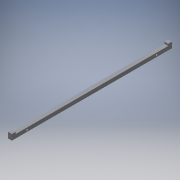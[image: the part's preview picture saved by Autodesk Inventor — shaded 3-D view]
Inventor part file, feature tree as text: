
AUTODESK INVENTOR PART (.ipt)
format: ipt  version: 2016 (Build 200138000, 138)  size: 125,440 bytes
history: native  units: in
note: dims shown in document units (in); Inventor stores cm internally (conversion verified against a paired STEP export)
features: sketch x2, extrude x1, hole x1, mirror x1
ambient origin geometry x8: Origin, YZ Plane, XZ Plane, XY Plane, X Axis, Y Axis, Z Axis, Center Point
bodies: Solid1 (feature_tree)
feature tree (5):
  extrude  "Extrusion1"  Depth=0.25in
  hole  "Hole3"  [1 undecoded]
  mirror  "Mirror3"
  sketch  "Sketch1"  dims[d1=0.5in d3=0.25in]
  sketch  "Sketch4"  dims[d4=10.0in d5=0.5in d10=0.5in d11=0.0in d32=0.23in d33=2.0in d34=0.25in d35=0.23in d36=0.75in d37=0.375in d38=0.25in d39=0.5635in d40=1.0in d41=0.8108in]
note: 1 required parameter value undecoded (feature->parameter linkage not recoverable at this tier; creation-order binding heuristic only, values carry confidence <= 0.55)
